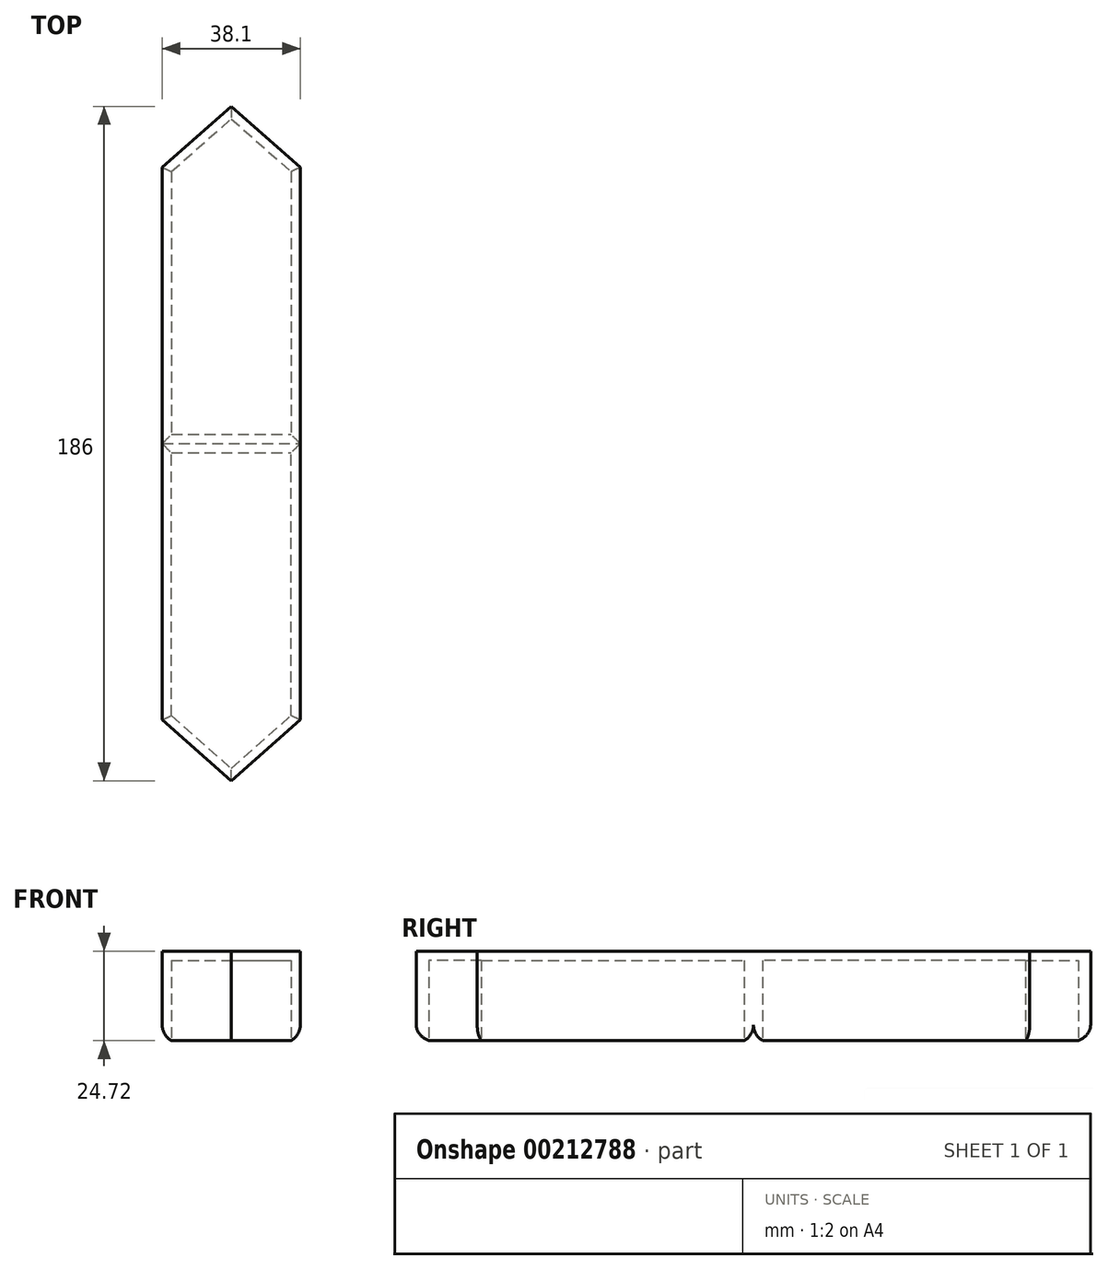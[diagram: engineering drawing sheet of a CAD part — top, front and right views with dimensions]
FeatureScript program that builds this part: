
annotation { "Feature Type Name" : "Feature", "Feature Type Description" : "" }
export const myFeature = defineFeature(function(context is Context, id is Id, definition is map)
    precondition{}
    {
        {
            var Q0;
            Q0=qCreatedBy(makeId("Top.planeOp"),FACE);
            var sketch = newSketch(context, id + "F0", { "sketchPlane" : qUnion([Q0])});
            skLineSegment(sketch, "E0.bottom", {"start": v(-13.1, -22.39) * mm, "end": v(25, -22.39) * mm});
            skLineSegment(sketch, "E0.top", {"start": v(-13.1, 53.81) * mm, "end": v(25, 53.81) * mm});
            skLineSegment(sketch, "E0.left", {"start": v(-13.1, -22.39) * mm, "end": v(-13.1, 53.81) * mm});
            skLineSegment(sketch, "E0.right", {"start": v(25, -22.39) * mm, "end": v(25, 53.81) * mm});
            skLineSegment(sketch, "E1", {"start": v(-13.1, -22.39) * mm, "end": v(5.96, -39.19) * mm});
            skLineSegment(sketch, "E2", {"start": v(5.96, -39.19) * mm, "end": v(25, -22.39) * mm});
            skSolve(sketch);
        }
        {
            var Q0;
            Q0=makeQuery(id+"F0.imprint","IMPRINT",FACE,{"disambiguationData":[TD([[makeQuery(id+"F0.imprint","IMPRINT",EDGE,{"derivedFrom":sQuery(id+"F0.wireOp",EDGE,"E0.bottom")}),-1.0]])]});
            extrude(context, id + "F1", {"entities" : qUnion([Q0]), "depth" : 25.4 * mm});
        }
        {
            var Q0;
            Q0=makeQuery(id+"F0.imprint","IMPRINT",FACE,{"disambiguationData":[TD([[makeQuery(id+"F0.imprint","IMPRINT",EDGE,{"derivedFrom":sQuery(id+"F0.wireOp",EDGE,"E0.bottom")}),1.0]])]});
            extrude(context, id + "F2", {"entities" : qUnion([Q0]), "operationType" : NewBodyOperationType.ADD, "depth" : 25.4 * mm});
        }
        {
            var Q0;
            {var subQ0=sQuery(id+"F0.wireOp",EDGE,"E0.bottom");Q0=makeQuery(id+"F2.boolean.opBoolean","MERGE",FACE,{"derivedFrom":[makeQuery(id+"F1.opExtrude","CAP_FACE",FACE,{"disambiguationData":[OSD([subQ0,sQuery(id+"F0.wireOp",EDGE,"E1"),sQuery(id+"F0.wireOp",EDGE,"E2")])],"isStart":true}),makeQuery(id+"F2.opExtrude","CAP_FACE",FACE,{"disambiguationData":[OSD([subQ0,sQuery(id+"F0.wireOp",EDGE,"E0.top"),sQuery(id+"F0.wireOp",EDGE,"E0.left"),sQuery(id+"F0.wireOp",EDGE,"E0.right")])],"isStart":true})]});}
            shell(context, id + "F3", {"entities" : qUnion([Q0]), "thickness" : 2.54 * mm});
        }
        {
            var Q0;
            Q0=makeQuery(id+"F2.opExtrude","CAP_EDGE",EDGE,{"disambiguationData":[OSD([sQuery(id+"F0.wireOp",EDGE,"E0.right")])],"isStart":true});
            var Q1;
            Q1=makeQuery(id+"F1.opExtrude","CAP_EDGE",EDGE,{"disambiguationData":[OSD([sQuery(id+"F0.wireOp",EDGE,"E2")])],"isStart":true});
            var Q2;
            Q2=makeQuery(id+"F1.opExtrude","CAP_EDGE",EDGE,{"disambiguationData":[OSD([sQuery(id+"F0.wireOp",EDGE,"E1")])],"isStart":true});
            var Q3;
            Q3=makeQuery(id+"F2.opExtrude","CAP_EDGE",EDGE,{"disambiguationData":[OSD([sQuery(id+"F0.wireOp",EDGE,"E0.left")])],"isStart":true});
            var Q4;
            Q4=makeQuery(id+"F2.opExtrude","CAP_EDGE",EDGE,{"disambiguationData":[OSD([sQuery(id+"F0.wireOp",EDGE,"E0.top")])],"isStart":true});
            fillet(context, id + "F4", {"entities" : qUnion([Q0, Q1, Q2, Q3, Q4]), "radius" : 5.08 * mm, "tangentPropagation" : true, "allowEdgeOverflow" : false});
        }
        {
            var Q0;
            Q0=makeQuery(id+"F1.opExtrude","SWEPT_BODY",BODY,{"disambiguationData":[OSD([sQuery(id+"F0.wireOp",EDGE,"E0.bottom"),sQuery(id+"F0.wireOp",EDGE,"E1"),sQuery(id+"F0.wireOp",EDGE,"E2")])]});
            var Q1;
            Q1=makeQuery(id+"F2.opExtrude","SWEPT_FACE",FACE,{"disambiguationData":[OSD([sQuery(id+"F0.wireOp",EDGE,"E0.top")])]});
            mirror(context, id + "F5", {"operationType" : NewBodyOperationType.ADD, "entities" : qUnion([Q0]), "mirrorPlane" : qUnion([Q1])});
        }
    });
